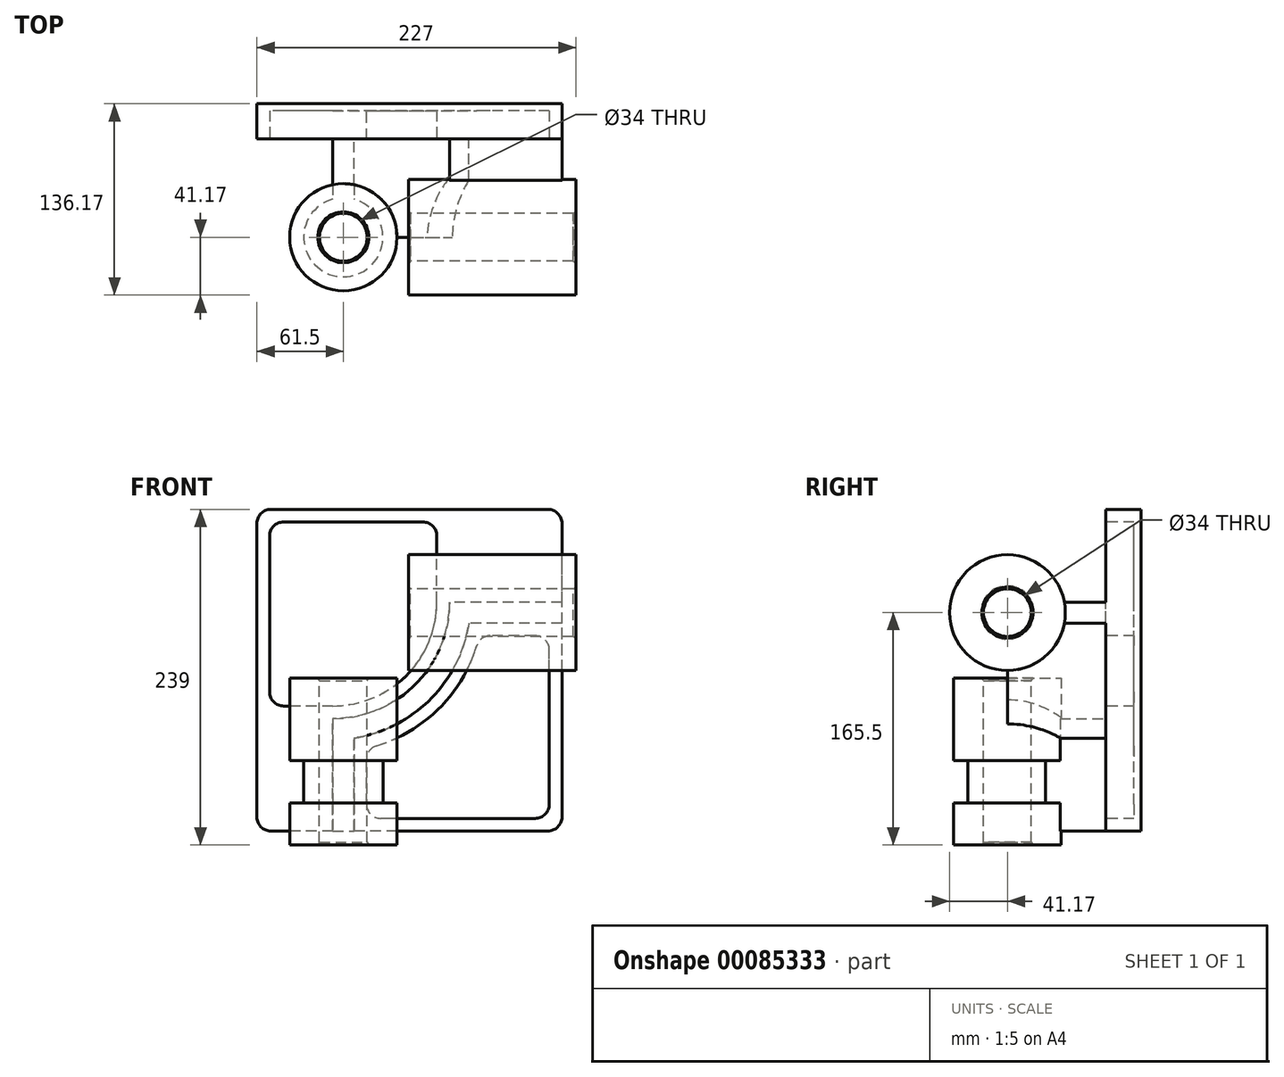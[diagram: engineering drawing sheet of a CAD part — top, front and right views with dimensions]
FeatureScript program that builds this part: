
annotation { "Feature Type Name" : "Feature", "Feature Type Description" : "" }
export const myFeature = defineFeature(function(context is Context, id is Id, definition is map)
    precondition{}
    {
        {
            var Q0;
            Q0=qCreatedBy(makeId("Front.planeOp"),FACE);
            var sketch = newSketch(context, id + "F0", { "sketchPlane" : qUnion([Q0])});
            skLineSegment(sketch, "E0.bottom", {"start": v(0, 0) * mm, "end": v(-217, 0) * mm});
            skLineSegment(sketch, "E0.top", {"start": v(0, 229) * mm, "end": v(-217, 229) * mm});
            skLineSegment(sketch, "E0.left", {"start": v(0, 0) * mm, "end": v(0, 229) * mm});
            skLineSegment(sketch, "E0.right", {"start": v(-217, 0) * mm, "end": v(-217, 229) * mm});
            skSolve(sketch);
        }
        {
            var Q0;
            Q0 = qSketchRegion(id + "F0", true);
            extrude(context, id + "F1", {"entities" : qUnion([Q0]), "depth" : 25 * mm});
        }
        {
            var Q0;
            Q0=makeQuery(id+"F1.opExtrude","CAP_FACE",FACE,{"disambiguationData":[OSD([sQuery(id+"F0.wireOp",EDGE,"E0.bottom"),sQuery(id+"F0.wireOp",EDGE,"E0.top"),sQuery(id+"F0.wireOp",EDGE,"E0.left"),sQuery(id+"F0.wireOp",EDGE,"E0.right")])],"isStart":false});
            var sketch = newSketch(context, id + "F2", { "sketchPlane" : qUnion([Q0])});
            skLineSegment(sketch, "E1", {"start": v(-148, 0) * mm, "end": v(-148, 66.15) * mm});
            skLineSegment(sketch, "E2", {"start": v(0, 148) * mm, "end": v(-66.15, 148) * mm});
            skArc(sketch, "E3", {"start": v(-66.15, 148) * mm, "mid": v(-93.7, 93.7) * mm, "end": v(-148, 66.15) * mm});
            skLineSegment(sketch, "E4.0", {"start": v(-163, 0) * mm, "end": v(-163, 80) * mm});
            skArc(sketch, "E4.1", {"start": v(-80, 163) * mm, "mid": v(-104.31, 104.31) * mm, "end": v(-163, 80) * mm});
            skLineSegment(sketch, "E4.2", {"start": v(0, 163) * mm, "end": v(-80, 163) * mm});
            skLineSegment(sketch, "E5.0", {"start": v(0, 229) * mm, "end": v(-217, 229) * mm});
            skLineSegment(sketch, "E5.1", {"start": v(-217, 0) * mm, "end": v(-217, 229) * mm});
            skLineSegment(sketch, "E5.2", {"start": v(0, 0) * mm, "end": v(-217, 0) * mm});
            skLineSegment(sketch, "E5.3", {"start": v(0, 0) * mm, "end": v(0, 229) * mm});
            skSolve(sketch);
        }
        {
            var Q0;
            {var subQ2=sQuery(id+"F2.wireOp",EDGE,"E1");Q0=makeQuery(id+"F2.imprint","IMPRINT",FACE,{"disambiguationData":[TD([[makeQuery(id+"F2.imprint","IMPRINT",EDGE,{"derivedFrom":subQ2}),1.0]])]});}
            extrude(context, id + "F3", {"entities" : qUnion([Q0]), "operationType" : NewBodyOperationType.ADD, "depth" : 70 * mm});
        }
        {
            var Q0;
            {var subQ0=sQuery(id+"F0.wireOp",EDGE,"E0.left");var subQ1=sQuery(id+"F0.wireOp",EDGE,"E0.bottom");Q0=makeQuery(id+"F3.boolean.opBoolean","SPLIT",FACE,{"disambiguationData":[TD([makeQuery(id+"F3.opExtrude","SWEPT_FACE",FACE,{"disambiguationData":[OSD([sQuery(id+"F2.wireOp",EDGE,"E1")])]})])],"derivedFrom":makeQuery(id+"F1.opExtrude","CAP_FACE",FACE,{"disambiguationData":[OSD([subQ1,sQuery(id+"F0.wireOp",EDGE,"E0.top"),subQ0,sQuery(id+"F0.wireOp",EDGE,"E0.right")])],"isStart":false})});}
            var sketch = newSketch(context, id + "F4", { "sketchPlane" : qUnion([Q0])});
            skLineSegment(sketch, "E6.0", {"start": v(-9, 139) * mm, "end": v(-58.73, 139) * mm});
            skLineSegment(sketch, "E6.1", {"start": v(-9, 9) * mm, "end": v(-9, 139) * mm});
            skArc(sketch, "E6.2", {"start": v(-58.73, 139) * mm, "mid": v(-87.34, 87.34) * mm, "end": v(-139, 58.73) * mm});
            skLineSegment(sketch, "E6.3", {"start": v(-139, 9) * mm, "end": v(-139, 58.73) * mm});
            skLineSegment(sketch, "E6.4", {"start": v(-9, 9) * mm, "end": v(-139, 9) * mm});
            skLineSegment(sketch, "E7.0", {"start": v(-80, 229) * mm, "end": v(-217, 229) * mm});
            skLineSegment(sketch, "E7.1", {"start": v(-217, 80) * mm, "end": v(-217, 229) * mm});
            skArc(sketch, "E7.2", {"start": v(-80, 163) * mm, "mid": v(-104.31, 104.31) * mm, "end": v(-163, 80) * mm});
            skLineSegment(sketch, "E8", {"start": v(-80, 163) * mm, "end": v(-80, 229) * mm});
            skLineSegment(sketch, "E9", {"start": v(-163, 80) * mm, "end": v(-217, 80) * mm});
            skPoint(sketch, "E10.orphan", {"position": v(0, 229) * mm});
            skPoint(sketch, "E11.orphan", {"position": v(-217, 0) * mm});
            skLineSegment(sketch, "E12.0", {"start": v(-208, 89) * mm, "end": v(-208, 220) * mm});
            skLineSegment(sketch, "E12.1", {"start": v(-89, 220) * mm, "end": v(-208, 220) * mm});
            skLineSegment(sketch, "E12.2", {"start": v(-163, 89) * mm, "end": v(-208, 89) * mm});
            skArc(sketch, "E12.3", {"start": v(-89, 163) * mm, "mid": v(-110.67, 110.67) * mm, "end": v(-163, 89) * mm});
            skLineSegment(sketch, "E12.4", {"start": v(-89, 163) * mm, "end": v(-89, 220) * mm});
            skSolve(sketch);
        }
        {
            var Q0;
            Q0=makeQuery(id+"F4.imprint","IMPRINT",FACE,{"disambiguationData":[TD([[makeQuery(id+"F4.imprint","IMPRINT",EDGE,{"derivedFrom":sQuery(id+"F4.wireOp",EDGE,"E12.0")}),-1.0]])]});
            var Q1;
            Q1=makeQuery(id+"F4.imprint","IMPRINT",FACE,{"disambiguationData":[TD([[makeQuery(id+"F4.imprint","IMPRINT",EDGE,{"derivedFrom":sQuery(id+"F4.wireOp",EDGE,"E6.0")}),1.0]])]});
            extrude(context, id + "F5", {"entities" : qUnion([Q0, Q1]), "operationType" : NewBodyOperationType.REMOVE, "oppositeDirection" : true, "depth" : 20 * mm});
        }
        {
            var Q0;
            Q0=makeQuery(id+"F3.boolean.opBoolean","MERGE",FACE,{"derivedFrom":[makeQuery(id+"F1.opExtrude","SWEPT_FACE",FACE,{"disambiguationData":[OSD([sQuery(id+"F0.wireOp",EDGE,"E0.left")])]}),makeQuery(id+"F3.opExtrude","SWEPT_FACE",FACE,{"disambiguationData":[OSD([sQuery(id+"F2.wireOp",EDGE,"E5.3")])]})]});
            var sketch = newSketch(context, id + "F6", { "sketchPlane" : qUnion([Q0])});
            skLineSegment(sketch, "E13.0", {"start": v(-95, 148) * mm, "end": v(-95, 163) * mm});
            skCircle(sketch, "E14", {"center": v(-95, 155.5) * mm, "radius": 17 * mm});
            skCircle(sketch, "E15", {"center": v(-95, 155.5) * mm, "radius": 41.17 * mm});
            skSolve(sketch);
        }
        {
            var Q0;
            Q0=makeQuery(id+"F3.boolean.opBoolean","MERGE",FACE,{"derivedFrom":[makeQuery(id+"F1.opExtrude","SWEPT_FACE",FACE,{"disambiguationData":[OSD([sQuery(id+"F0.wireOp",EDGE,"E0.bottom")])]}),makeQuery(id+"F3.opExtrude","SWEPT_FACE",FACE,{"disambiguationData":[OSD([sQuery(id+"F2.wireOp",EDGE,"E5.2")])]})]});
            var sketch = newSketch(context, id + "F7", { "sketchPlane" : qUnion([Q0])});
            skLineSegment(sketch, "E16.0", {"start": v(-148, 95) * mm, "end": v(-163, 95) * mm});
            skCircle(sketch, "E17", {"center": v(-155.5, 95) * mm, "radius": 38.17 * mm});
            skCircle(sketch, "E18", {"center": v(-155.5, 95) * mm, "radius": 17 * mm});
            skSolve(sketch);
        }
        {
            var Q0;
            {var subQ0=sQuery(id+"F7.wireOp",EDGE,"E17");var subQ1=sQuery(id+"F2.wireOp",EDGE,"E5.2");var subQ2=makeQuery(id+"F3.opExtrude","SWEPT_EDGE",EDGE,{"disambiguationData":[OSD([sQuery(id+"F2.wireOp",EDGE,"E1"),subQ1])]});var subQ3=makeQuery(id+"F7.imprint","INTERSECT",VERTEX,{"derivedFrom":[subQ2,subQ0]});Q0=makeQuery(id+"F7.imprint","IMPRINT",FACE,{"disambiguationData":[TD([[makeQuery(id+"F7.imprint","IMPRINT",EDGE,{"disambiguationData":[TD([[subQ3,1.0]])],"derivedFrom":subQ0}),1.0]])]});}
            var Q1;
            {var subQ0=sQuery(id+"F7.wireOp",EDGE,"E16.0");Q1=makeQuery(id+"F7.imprint","IMPRINT",FACE,{"disambiguationData":[TD([[makeQuery(id+"F7.imprint","IMPRINT",EDGE,{"derivedFrom":subQ0}),1.0]])]});}
            var Q2;
            {var subQ0=sQuery(id+"F7.wireOp",EDGE,"E16.0");Q2=makeQuery(id+"F7.imprint","IMPRINT",FACE,{"disambiguationData":[TD([[makeQuery(id+"F7.imprint","IMPRINT",EDGE,{"derivedFrom":subQ0}),-1.0]])]});}
            var Q3;
            {var subQ0=sQuery(id+"F7.wireOp",EDGE,"E17");var subQ1=sQuery(id+"F2.wireOp",EDGE,"E5.2");var subQ2=makeQuery(id+"F3.opExtrude","SWEPT_EDGE",EDGE,{"disambiguationData":[OSD([sQuery(id+"F2.wireOp",EDGE,"E1"),subQ1])]});var subQ3=makeQuery(id+"F7.imprint","INTERSECT",VERTEX,{"derivedFrom":[subQ2,subQ0]});Q3=makeQuery(id+"F7.imprint","IMPRINT",FACE,{"disambiguationData":[TD([[makeQuery(id+"F7.imprint","IMPRINT",EDGE,{"disambiguationData":[TD([[subQ3,-1.0]])],"derivedFrom":subQ0}),1.0]])]});}
            extrude(context, id + "F8", {"entities" : qUnion([Q0, Q1, Q2, Q3]), "operationType" : NewBodyOperationType.ADD, "oppositeDirection" : true, "depth" : 109 * mm});
        }
        {
            var Q0;
            {var subQ0=sQuery(id+"F6.wireOp",EDGE,"E13.0");Q0=makeQuery(id+"F6.imprint","IMPRINT",FACE,{"disambiguationData":[TD([[makeQuery(id+"F6.imprint","IMPRINT",EDGE,{"derivedFrom":subQ0}),-1.0]])]});}
            var Q1;
            {var subQ0=sQuery(id+"F6.wireOp",EDGE,"E13.0");Q1=makeQuery(id+"F6.imprint","IMPRINT",FACE,{"disambiguationData":[TD([[makeQuery(id+"F6.imprint","IMPRINT",EDGE,{"derivedFrom":subQ0}),1.0]])]});}
            var Q2;
            {var subQ0=sQuery(id+"F6.wireOp",EDGE,"E14");var subQ1=sQuery(id+"F2.wireOp",EDGE,"E5.3");var subQ2=makeQuery(id+"F3.opExtrude","SWEPT_EDGE",EDGE,{"disambiguationData":[OSD([sQuery(id+"F2.wireOp",EDGE,"E2"),subQ1])]});var subQ3=makeQuery(id+"F6.imprint","INTERSECT",VERTEX,{"derivedFrom":[subQ2,subQ0]});Q2=makeQuery(id+"F6.imprint","IMPRINT",FACE,{"disambiguationData":[TD([[makeQuery(id+"F6.imprint","IMPRINT",EDGE,{"disambiguationData":[TD([[subQ3,-1.0]])],"derivedFrom":subQ0}),-1.0]])]});}
            var Q3;
            {var subQ0=sQuery(id+"F6.wireOp",EDGE,"E14");var subQ1=sQuery(id+"F2.wireOp",EDGE,"E5.3");var subQ2=makeQuery(id+"F3.opExtrude","SWEPT_EDGE",EDGE,{"disambiguationData":[OSD([sQuery(id+"F2.wireOp",EDGE,"E2"),subQ1])]});var subQ3=makeQuery(id+"F6.imprint","INTERSECT",VERTEX,{"derivedFrom":[subQ2,subQ0]});Q3=makeQuery(id+"F6.imprint","IMPRINT",FACE,{"disambiguationData":[TD([[makeQuery(id+"F6.imprint","IMPRINT",EDGE,{"disambiguationData":[TD([[subQ3,1.0]])],"derivedFrom":subQ0}),-1.0]])]});}
            extrude(context, id + "F9", {"entities" : qUnion([Q0, Q1, Q2, Q3]), "operationType" : NewBodyOperationType.ADD, "oppositeDirection" : true, "depth" : 109 * mm});
        }
        {
            var Q0;
            {var subQ0=sQuery(id+"F7.wireOp",EDGE,"E17");var subQ1=sQuery(id+"F2.wireOp",EDGE,"E5.2");var subQ2=makeQuery(id+"F3.opExtrude","SWEPT_EDGE",EDGE,{"disambiguationData":[OSD([sQuery(id+"F2.wireOp",EDGE,"E1"),subQ1])]});var subQ3=makeQuery(id+"F7.imprint","INTERSECT",VERTEX,{"derivedFrom":[subQ2,subQ0]});Q0=makeQuery(id+"F7.imprint","IMPRINT",FACE,{"disambiguationData":[TD([[makeQuery(id+"F7.imprint","IMPRINT",EDGE,{"disambiguationData":[TD([[subQ3,-1.0]])],"derivedFrom":subQ0}),1.0]])]});}
            var Q1;
            {var subQ0=sQuery(id+"F7.wireOp",EDGE,"E17");var subQ1=sQuery(id+"F2.wireOp",EDGE,"E5.2");var subQ2=makeQuery(id+"F3.opExtrude","SWEPT_EDGE",EDGE,{"disambiguationData":[OSD([sQuery(id+"F2.wireOp",EDGE,"E1"),subQ1])]});var subQ3=makeQuery(id+"F7.imprint","INTERSECT",VERTEX,{"derivedFrom":[subQ2,subQ0]});Q1=makeQuery(id+"F7.imprint","IMPRINT",FACE,{"disambiguationData":[TD([[makeQuery(id+"F7.imprint","IMPRINT",EDGE,{"disambiguationData":[TD([[subQ3,1.0]])],"derivedFrom":subQ0}),1.0]])]});}
            extrude(context, id + "F10", {"entities" : qUnion([Q0, Q1]), "operationType" : NewBodyOperationType.ADD, "depth" : 10 * mm});
        }
        {
            var Q0;
            {var subQ0=sQuery(id+"F6.wireOp",EDGE,"E14");var subQ1=sQuery(id+"F2.wireOp",EDGE,"E5.3");var subQ2=makeQuery(id+"F3.opExtrude","SWEPT_EDGE",EDGE,{"disambiguationData":[OSD([sQuery(id+"F2.wireOp",EDGE,"E2"),subQ1])]});var subQ3=makeQuery(id+"F6.imprint","INTERSECT",VERTEX,{"derivedFrom":[subQ2,subQ0]});Q0=makeQuery(id+"F6.imprint","IMPRINT",FACE,{"disambiguationData":[TD([[makeQuery(id+"F6.imprint","IMPRINT",EDGE,{"disambiguationData":[TD([[subQ3,-1.0]])],"derivedFrom":subQ0}),-1.0]])]});}
            var Q1;
            {var subQ0=sQuery(id+"F6.wireOp",EDGE,"E14");var subQ1=sQuery(id+"F2.wireOp",EDGE,"E5.3");var subQ2=makeQuery(id+"F3.opExtrude","SWEPT_EDGE",EDGE,{"disambiguationData":[OSD([sQuery(id+"F2.wireOp",EDGE,"E2"),subQ1])]});var subQ3=makeQuery(id+"F6.imprint","INTERSECT",VERTEX,{"derivedFrom":[subQ2,subQ0]});Q1=makeQuery(id+"F6.imprint","IMPRINT",FACE,{"disambiguationData":[TD([[makeQuery(id+"F6.imprint","IMPRINT",EDGE,{"disambiguationData":[TD([[subQ3,1.0]])],"derivedFrom":subQ0}),-1.0]])]});}
            extrude(context, id + "F11", {"entities" : qUnion([Q0, Q1]), "operationType" : NewBodyOperationType.ADD, "depth" : 10 * mm});
        }
        {
            var Q0;
            {var subQ0=sQuery(id+"F6.wireOp",EDGE,"E13.0");Q0=makeQuery(id+"F6.imprint","IMPRINT",FACE,{"disambiguationData":[TD([[makeQuery(id+"F6.imprint","IMPRINT",EDGE,{"derivedFrom":subQ0}),1.0]])]});}
            var Q1;
            {var subQ0=sQuery(id+"F6.wireOp",EDGE,"E13.0");Q1=makeQuery(id+"F6.imprint","IMPRINT",FACE,{"disambiguationData":[TD([[makeQuery(id+"F6.imprint","IMPRINT",EDGE,{"derivedFrom":subQ0}),-1.0]])]});}
            extrude(context, id + "F12", {"entities" : qUnion([Q0, Q1]), "operationType" : NewBodyOperationType.REMOVE, "endBound" : BoundingType.THROUGH_ALL, "oppositeDirection" : true, "depth" : 25 * mm});
        }
        {
            var Q0;
            {var subQ0=sQuery(id+"F7.wireOp",EDGE,"E16.0");Q0=makeQuery(id+"F7.imprint","IMPRINT",FACE,{"disambiguationData":[TD([[makeQuery(id+"F7.imprint","IMPRINT",EDGE,{"derivedFrom":subQ0}),-1.0]])]});}
            var Q1;
            {var subQ0=sQuery(id+"F7.wireOp",EDGE,"E16.0");Q1=makeQuery(id+"F7.imprint","IMPRINT",FACE,{"disambiguationData":[TD([[makeQuery(id+"F7.imprint","IMPRINT",EDGE,{"derivedFrom":subQ0}),1.0]])]});}
            extrude(context, id + "F13", {"entities" : qUnion([Q0, Q1]), "operationType" : NewBodyOperationType.REMOVE, "endBound" : BoundingType.THROUGH_ALL, "oppositeDirection" : true, "depth" : 25 * mm});
        }
        {
            var Q0;
            Q0=makeQuery(id+"F10.opExtrude","CAP_FACE",FACE,{"disambiguationData":[OSD([sQuery(id+"F7.wireOp",EDGE,"E17"),sQuery(id+"F7.wireOp",EDGE,"E18")])],"isStart":false});
            cPlane(context, id + "F14", {"entities" : qUnion([Q0]), "cplaneType" : CPlaneType.OFFSET, "offset" : 30 * mm, "oppositeDirection" : true, "width" : 150 * mm, "height" : 150 * mm});
        }
        {
            var Q0;
            Q0=qCreatedBy(id+"F14.planeOp",FACE);
            var sketch = newSketch(context, id + "F15", { "sketchPlane" : qUnion([Q0])});
            skArc(sketch, "E19.0", {"start": v(-148, 57.58) * mm, "mid": v(-155.5, 133.17) * mm, "end": v(-163, 57.58) * mm});
            skArc(sketch, "E20", {"start": v(-148, 67.85) * mm, "mid": v(-155.5, 123.17) * mm, "end": v(-163, 67.85) * mm});
            skLineSegment(sketch, "E21", {"start": v(-163, 57.58) * mm, "end": v(-163, 67.85) * mm});
            skLineSegment(sketch, "E22", {"start": v(-148, 57.58) * mm, "end": v(-148, 67.85) * mm});
            skPoint(sketch, "E23.1.end.orphan", {"position": v(-148, 25) * mm});
            skPoint(sketch, "E23.0.end.orphan", {"position": v(-163, 25) * mm});
            skSolve(sketch);
        }
        {
            var Q0;
            Q0 = qSketchRegion(id + "F15", true);
            extrude(context, id + "F16", {"entities" : qUnion([Q0]), "operationType" : NewBodyOperationType.REMOVE, "oppositeDirection" : true, "depth" : 30 * mm});
        }
        {
            var Q0;
            Q0=makeQuery(id+"F10.opExtrude","CAP_EDGE",EDGE,{"disambiguationData":[OSD([sQuery(id+"F7.wireOp",EDGE,"E18")])],"isStart":false});
            var Q1;
            Q1=makeQuery(id+"F11.opExtrude","CAP_EDGE",EDGE,{"disambiguationData":[OSD([sQuery(id+"F6.wireOp",EDGE,"E14")])],"isStart":false});
            var Q2;
            Q2=makeQuery(id+"F13.boolean.opBoolean","INTERSECT",EDGE,{"derivedFrom":[makeQuery(id+"F8.opExtrude","CAP_FACE",FACE,{"disambiguationData":[OSD([sQuery(id+"F7.wireOp",EDGE,"E17")])],"isStart":false}),makeQuery(id+"F13.opExtrude","SWEPT_FACE",FACE,{"disambiguationData":[OSD([sQuery(id+"F7.wireOp",EDGE,"E18")])]})]});
            var Q3;
            Q3=makeQuery(id+"F12.boolean.opBoolean","INTERSECT",EDGE,{"derivedFrom":[makeQuery(id+"F9.opExtrude","CAP_FACE",FACE,{"disambiguationData":[OSD([sQuery(id+"F6.wireOp",EDGE,"E15")])],"isStart":false}),makeQuery(id+"F12.opExtrude","SWEPT_FACE",FACE,{"disambiguationData":[OSD([sQuery(id+"F6.wireOp",EDGE,"E14")])]})]});
            chamfer(context, id + "F17", {"entities" : qUnion([Q0, Q1, Q2, Q3]), "chamferType" : ChamferType.OFFSET_ANGLE, "width" : 2 * mm, "oppositeDirection" : false, "angle" : 30 * degree});
        }
        {
            var Q0;
            Q0=makeQuery(id+"F1.opExtrude","SWEPT_EDGE",EDGE,{"disambiguationData":[OSD([sQuery(id+"F0.wireOp",EDGE,"E0.bottom"),sQuery(id+"F0.wireOp",EDGE,"E0.right")])]});
            var Q1;
            Q1=makeQuery(id+"F1.opExtrude","SWEPT_EDGE",EDGE,{"disambiguationData":[OSD([sQuery(id+"F0.wireOp",EDGE,"E0.bottom"),sQuery(id+"F0.wireOp",EDGE,"E0.left")])]});
            var Q2;
            Q2=makeQuery(id+"F1.opExtrude","SWEPT_EDGE",EDGE,{"disambiguationData":[OSD([sQuery(id+"F0.wireOp",EDGE,"E0.top"),sQuery(id+"F0.wireOp",EDGE,"E0.left")])]});
            var Q3;
            Q3=makeQuery(id+"F1.opExtrude","SWEPT_EDGE",EDGE,{"disambiguationData":[OSD([sQuery(id+"F0.wireOp",EDGE,"E0.top"),sQuery(id+"F0.wireOp",EDGE,"E0.right")])]});
            var Q4;
            Q4=makeQuery(id+"F5.boolean.opBoolean","COPY",EDGE,{"derivedFrom":makeQuery(id+"F5.opExtrude","SWEPT_EDGE",EDGE,{"disambiguationData":[OSD([sQuery(id+"F4.wireOp",EDGE,"E6.3"),sQuery(id+"F4.wireOp",EDGE,"E6.4")])]})});
            var Q5;
            Q5=makeQuery(id+"F5.boolean.opBoolean","COPY",EDGE,{"derivedFrom":makeQuery(id+"F5.opExtrude","SWEPT_EDGE",EDGE,{"disambiguationData":[OSD([sQuery(id+"F4.wireOp",EDGE,"E6.2"),sQuery(id+"F4.wireOp",EDGE,"E6.3")])]})});
            var Q6;
            Q6=makeQuery(id+"F5.boolean.opBoolean","COPY",EDGE,{"derivedFrom":makeQuery(id+"F5.opExtrude","SWEPT_EDGE",EDGE,{"disambiguationData":[OSD([sQuery(id+"F4.wireOp",EDGE,"E6.0"),sQuery(id+"F4.wireOp",EDGE,"E6.2")])]})});
            var Q7;
            Q7=makeQuery(id+"F5.boolean.opBoolean","COPY",EDGE,{"derivedFrom":makeQuery(id+"F5.opExtrude","SWEPT_EDGE",EDGE,{"disambiguationData":[OSD([sQuery(id+"F4.wireOp",EDGE,"E6.1"),sQuery(id+"F4.wireOp",EDGE,"E6.4")])]})});
            var Q8;
            Q8=makeQuery(id+"F5.boolean.opBoolean","COPY",EDGE,{"derivedFrom":makeQuery(id+"F5.opExtrude","SWEPT_EDGE",EDGE,{"disambiguationData":[OSD([sQuery(id+"F4.wireOp",EDGE,"E6.0"),sQuery(id+"F4.wireOp",EDGE,"E6.1")])]})});
            var Q9;
            Q9=makeQuery(id+"F5.boolean.opBoolean","COPY",EDGE,{"derivedFrom":makeQuery(id+"F5.opExtrude","SWEPT_EDGE",EDGE,{"disambiguationData":[OSD([sQuery(id+"F4.wireOp",EDGE,"E12.0"),sQuery(id+"F4.wireOp",EDGE,"E12.2")])]})});
            var Q10;
            Q10=makeQuery(id+"F5.boolean.opBoolean","COPY",EDGE,{"derivedFrom":makeQuery(id+"F5.opExtrude","SWEPT_EDGE",EDGE,{"disambiguationData":[OSD([sQuery(id+"F4.wireOp",EDGE,"E12.0"),sQuery(id+"F4.wireOp",EDGE,"E12.1")])]})});
            var Q11;
            Q11=makeQuery(id+"F5.boolean.opBoolean","COPY",EDGE,{"derivedFrom":makeQuery(id+"F5.opExtrude","SWEPT_EDGE",EDGE,{"disambiguationData":[OSD([sQuery(id+"F4.wireOp",EDGE,"E12.1"),sQuery(id+"F4.wireOp",EDGE,"E12.4")])]})});
            fillet(context, id + "F18", {"entities" : qUnion([Q0, Q1, Q2, Q3, Q4, Q5, Q6, Q7, Q8, Q9, Q10, Q11]), "radius" : 10 * mm, "tangentPropagation" : true, "allowEdgeOverflow" : false});
        }
    });
